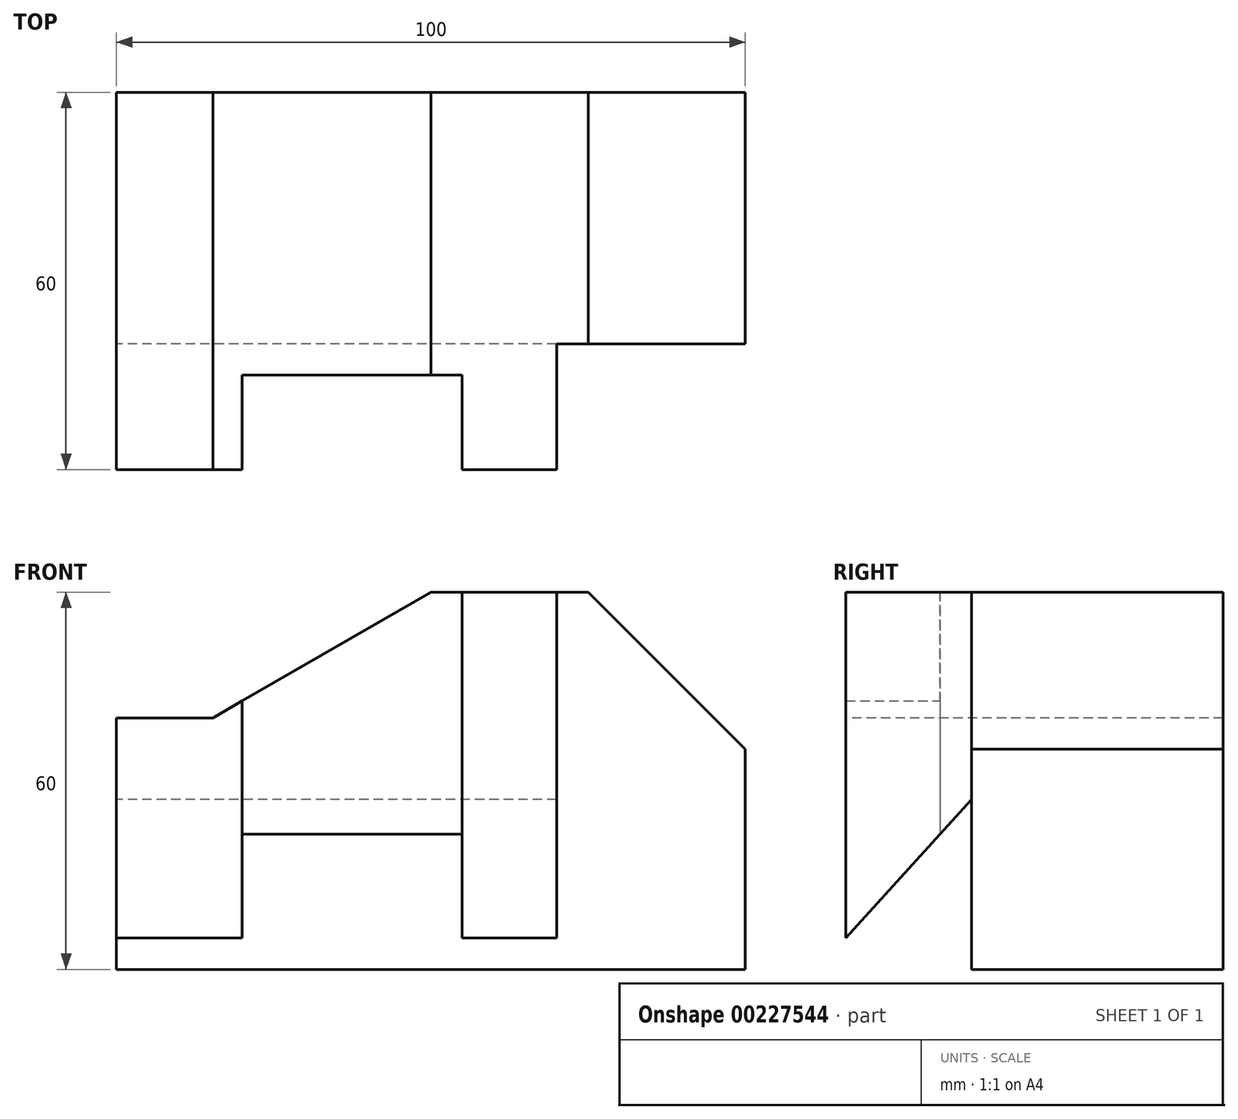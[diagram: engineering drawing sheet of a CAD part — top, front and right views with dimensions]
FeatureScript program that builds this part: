
annotation { "Feature Type Name" : "Feature", "Feature Type Description" : "" }
export const myFeature = defineFeature(function(context is Context, id is Id, definition is map)
    precondition{}
    {
        {
            var Q0;
            Q0=qCreatedBy(makeId("Top.planeOp"),FACE);
            var sketch = newSketch(context, id + "F0", { "sketchPlane" : qUnion([Q0])});
            skLineSegment(sketch, "E0", {"start": v(0, 0) * mm, "end": v(0, 60) * mm});
            skLineSegment(sketch, "E1", {"start": v(0, 60) * mm, "end": v(100, 60) * mm});
            skLineSegment(sketch, "E2", {"start": v(100, 60) * mm, "end": v(100, 20) * mm});
            skLineSegment(sketch, "E3", {"start": v(100, 20) * mm, "end": v(70, 20) * mm});
            skLineSegment(sketch, "E4", {"start": v(70, 20) * mm, "end": v(70, 0) * mm});
            skLineSegment(sketch, "E5", {"start": v(70, 0) * mm, "end": v(55, 0) * mm});
            skLineSegment(sketch, "E6", {"start": v(55, 0) * mm, "end": v(55, 15) * mm});
            skLineSegment(sketch, "E7", {"start": v(55, 15) * mm, "end": v(20, 15) * mm});
            skLineSegment(sketch, "E8", {"start": v(20, 15) * mm, "end": v(20, 0) * mm});
            skLineSegment(sketch, "E9", {"start": v(20, 0) * mm, "end": v(0, 0) * mm});
            skSolve(sketch);
        }
        {
            var Q0;
            Q0 = qSketchRegion(id + "F0", true);
            extrude(context, id + "F1", {"entities" : qUnion([Q0]), "depth" : 60 * mm});
        }
        {
            var Q0;
            Q0=qCreatedBy(makeId("Front.planeOp"),FACE);
            var sketch = newSketch(context, id + "F2", { "sketchPlane" : qUnion([Q0])});
            skLineSegment(sketch, "E10.0", {"start": v(55, 60) * mm, "end": v(20, 60) * mm, "construction": true});
            skLineSegment(sketch, "E11.0", {"start": v(20, 60) * mm, "end": v(0, 60) * mm, "construction": true});
            skLineSegment(sketch, "E12.0", {"start": v(0, 60) * mm, "end": v(0, 0) * mm, "construction": true});
            skPoint(sketch, "E13.0", {"position": v(85, 60) * mm});
            skLineSegment(sketch, "E14.0", {"start": v(100, 60) * mm, "end": v(70, 60) * mm, "construction": true});
            skLineSegment(sketch, "E15.0", {"start": v(100, 60) * mm, "end": v(100, 0) * mm, "construction": true});
            skLineSegment(sketch, "E16", {"start": v(50, 60) * mm, "end": v(0, 60) * mm});
            skLineSegment(sketch, "E17", {"start": v(0, 40) * mm, "end": v(15.36, 40) * mm});
            skLineSegment(sketch, "E18", {"start": v(15.36, 40) * mm, "end": v(50, 60) * mm});
            skLineSegment(sketch, "E19", {"start": v(75.03, 60) * mm, "end": v(100, 60) * mm});
            skLineSegment(sketch, "E20", {"start": v(100, 35.03) * mm, "end": v(75.03, 60) * mm});
            skLineSegment(sketch, "E21", {"start": v(100, 60) * mm, "end": v(100, 35.03) * mm});
            skLineSegment(sketch, "E22", {"start": v(0, 60) * mm, "end": v(0, 40) * mm});
            skSolve(sketch);
        }
        {
            var Q0;
            Q0=makeQuery(id+"F2.imprint","IMPRINT",FACE,{"disambiguationData":[TD([[makeQuery(id+"F2.imprint","IMPRINT",EDGE,{"derivedFrom":sQuery(id+"F2.wireOp",EDGE,"E19")}),-1.0]])]});
            var Q1;
            Q1=makeQuery(id+"F2.imprint","IMPRINT",FACE,{"disambiguationData":[TD([[makeQuery(id+"F2.imprint","IMPRINT",EDGE,{"derivedFrom":sQuery(id+"F2.wireOp",EDGE,"E16")}),1.0]])]});
            extrude(context, id + "F3", {"entities" : qUnion([Q0, Q1]), "operationType" : NewBodyOperationType.REMOVE, "endBound" : BoundingType.THROUGH_ALL, "oppositeDirection" : true, "depth" : 25 * mm});
        }
        {
            var Q0;
            Q0=qCreatedBy(makeId("Right.planeOp"),FACE);
            var sketch = newSketch(context, id + "F4", { "sketchPlane" : qUnion([Q0])});
            skLineSegment(sketch, "E23.0", {"start": v(60, 60) * mm, "end": v(20, 60) * mm});
            skPoint(sketch, "E24.0", {"position": v(15, 60) * mm});
            skLineSegment(sketch, "E25.0.0", {"start": v(0, 0) * mm, "end": v(20, 0) * mm});
            skLineSegment(sketch, "E25.0.1", {"start": v(20, 0) * mm, "end": v(20, 60) * mm});
            skLineSegment(sketch, "E25.0.2", {"start": v(20, 60) * mm, "end": v(0, 60) * mm});
            skLineSegment(sketch, "E25.0.3", {"start": v(0, 60) * mm, "end": v(0, 0) * mm});
            skLineSegment(sketch, "E26", {"start": v(50, 60) * mm, "end": v(0, 60) * mm});
            skLineSegment(sketch, "E27", {"start": v(0, 5) * mm, "end": v(50, 60) * mm});
            skSolve(sketch);
        }
        {
            var Q0;
            {var subQ0=sQuery(id+"F4.wireOp",EDGE,"E26");var subQ1=sQuery(id+"F4.wireOp",EDGE,"E25.0.1");var subQ2=makeQuery(id+"F4.imprint","INTERSECT",VERTEX,{"derivedFrom":[subQ1,subQ0]});Q0=makeQuery(id+"F4.imprint","IMPRINT",FACE,{"disambiguationData":[TD([[makeQuery(id+"F4.imprint","IMPRINT",EDGE,{"disambiguationData":[TD([[subQ2,1.0]])],"derivedFrom":subQ1}),-1.0]])]});}
            var Q1;
            {var subQ0=sQuery(id+"F4.wireOp",EDGE,"E26");var subQ1=sQuery(id+"F4.wireOp",EDGE,"E25.0.1");var subQ2=makeQuery(id+"F4.imprint","INTERSECT",VERTEX,{"derivedFrom":[subQ1,subQ0]});Q1=makeQuery(id+"F4.imprint","IMPRINT",FACE,{"disambiguationData":[TD([[makeQuery(id+"F4.imprint","IMPRINT",EDGE,{"disambiguationData":[TD([[subQ2,1.0]])],"derivedFrom":subQ1}),1.0]])]});}
            extrude(context, id + "F5", {"entities" : qUnion([Q0, Q1]), "operationType" : NewBodyOperationType.REMOVE, "endBound" : BoundingType.THROUGH_ALL, "depth" : 25 * mm});
        }
    });
